# Revit family: SL510 Slim_SlimECO 2-Flg. m.Seitenteile - Sturtzmontage_!!
name_source: partatom
category: Türen
revit_build: Autodesk Revit 2018 (Build: 20190510_1515(x64)
units: mm (PartAtom-declared; Revit-internal decimal feet)

## family parameters
Basisbauteil = Wand
Beim Laden mit Abzugskörper schneiden = Nein
Gemeinsam genutzt = Nein
Immer vertikal = Ja
OmniClass-Nummer = 23.30.10.00
OmniClass-Titel = Doors
Raumberechnungspunkt = Nein

## types (1)
- SL510 Slim_SlimECO 2-Flg. m.Seitenteile - Sturtzmontage_!!
    Dicke = 20 mm  [stored 0.0656168 ft]
    Familienversion = 1.0
    Glasstärke = 8 mm  [stored 0.0262467 ft]
    Höhe ab FBOK berechnen = Ja
    IFC_Glasflächenanteil = 0
    IFC_Luftdurchlässigkeit = 0
    IFC_Schallschutzklasse = 0
    Kollisionskörper = Nein
    Montagefuge Breite = 5 mm  [stored 0.0164042 ft]
    Wandabschluss = Nach Basisbauteil

note: [stored X ft] marks values corroborated as IEEE doubles in the binary element streams (Revit-internal decimal feet)
